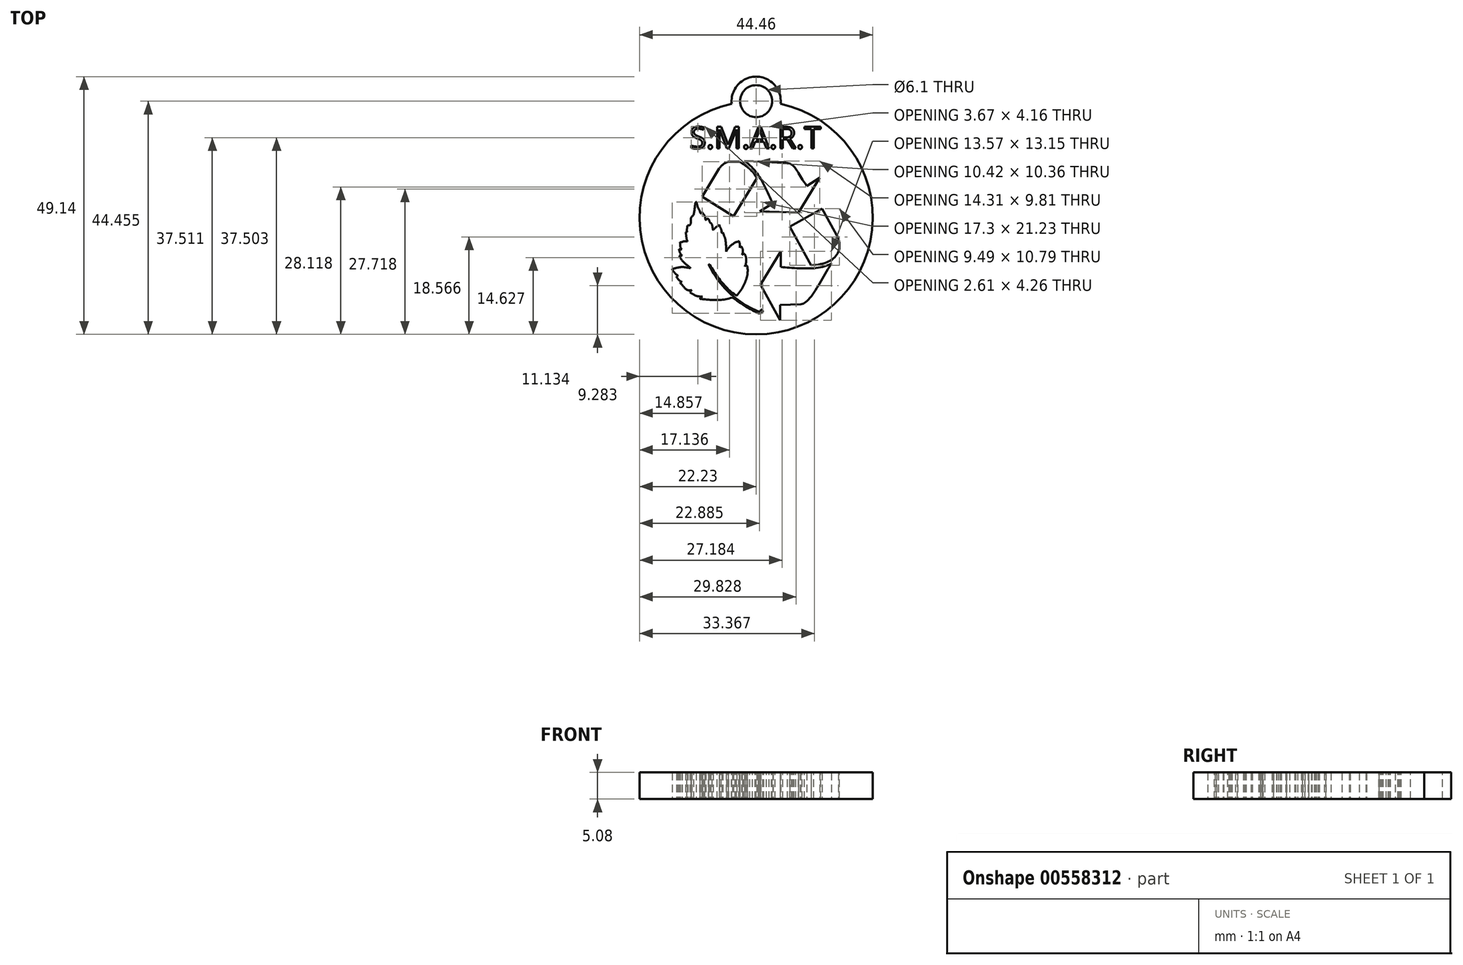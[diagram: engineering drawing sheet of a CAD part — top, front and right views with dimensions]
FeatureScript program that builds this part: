
annotation { "Feature Type Name" : "Feature", "Feature Type Description" : "" }
export const myFeature = defineFeature(function(context is Context, id is Id, definition is map)
    precondition{}
    {
        {
            var Q0;
            Q0=qCreatedBy(makeId("Top.planeOp"),FACE);
            var sketch = newSketch(context, id + "F0", { "sketchPlane" : qUnion([Q0])});
            skCircle(sketch, "E0", {"center": v(0, 0) * mm, "radius": 22.23 * mm});
            skLineSegment(sketch, "E1", {"start": v(4.56, -19.52) * mm, "end": v(4.56, -16.6) * mm});
            skLineSegment(sketch, "E2", {"start": v(4.56, -19.52) * mm, "end": v(0.81, -12.74) * mm});
            skLineSegment(sketch, "E3", {"start": v(0.81, -12.74) * mm, "end": v(4.68, -6.37) * mm});
            skLineSegment(sketch, "E4", {"start": v(4.68, -6.37) * mm, "end": v(4.68, -9.38) * mm});
            skFitSpline(sketch, "E5", {"points": [v(4.68, -9.38) * mm, v(14.38, -8.68) * mm], "startDerivative": vector(9.07, -0.86) * mm, "endDerivative": vector(6.6, 4.16) * mm});
            skFitSpline(sketch, "E6", {"points": [v(14.38, -8.68) * mm, v(8.52, -16.48) * mm], "startDerivative": vector(-5.26, -7.9) * mm, "endDerivative": vector(-5.23, 0.16) * mm});
            skLineSegment(sketch, "E7", {"start": v(8.52, -16.48) * mm, "end": v(4.56, -16.6) * mm});
            skLineSegment(sketch, "E8", {"start": v(10.48, -9.06) * mm, "end": v(6.4, -1.67) * mm});
            skLineSegment(sketch, "E9", {"start": v(6.4, -1.67) * mm, "end": v(12.54, 1.73) * mm});
            skFitSpline(sketch, "E10", {"points": [v(10.48, -9.06) * mm, v(15.66, -3.9) * mm], "startDerivative": vector(11.37, 0.62) * mm, "endDerivative": vector(-3, 9.99) * mm});
            skLineSegment(sketch, "E11", {"start": v(15.66, -3.9) * mm, "end": v(12.54, 1.73) * mm});
            skLineSegment(sketch, "E12", {"start": v(-10.3, 4) * mm, "end": v(-4.31, 0.3) * mm});
            skLineSegment(sketch, "E13", {"start": v(-4.31, 0.3) * mm, "end": v(0.12, 7.49) * mm});
            skFitSpline(sketch, "E14", {"points": [v(0.12, 7.49) * mm, v(-3.15, 10.67) * mm], "startDerivative": vector(-1.7, 4.08) * mm, "endDerivative": vector(-4.05, 2.48) * mm});
            skLineSegment(sketch, "E15", {"start": v(-3.15, 10.67) * mm, "end": v(-5.34, 10.67) * mm});
            skFitSpline(sketch, "E16", {"points": [v(-5.34, 10.67) * mm, v(-7.03, 9.39) * mm], "startDerivative": vector(-1.77, -0.76) * mm, "endDerivative": vector(-1.77, -2.58) * mm});
            skLineSegment(sketch, "E17", {"start": v(-7.03, 9.39) * mm, "end": v(-10.3, 4) * mm});
            skLineSegment(sketch, "E18", {"start": v(3.14, 2.73) * mm, "end": v(0.67, 1.2) * mm});
            skLineSegment(sketch, "E19", {"start": v(0.67, 1.2) * mm, "end": v(8.09, 0.98) * mm});
            skLineSegment(sketch, "E20", {"start": v(8.09, 0.98) * mm, "end": v(12.1, 7.65) * mm});
            skLineSegment(sketch, "E21", {"start": v(12.1, 7.65) * mm, "end": v(9.67, 6.06) * mm});
            skFitSpline(sketch, "E22", {"points": [v(3.14, 2.73) * mm, v(-2.2, 10.8) * mm], "startDerivative": vector(-4.28, 9.41) * mm, "endDerivative": vector(-8.22, 5.58) * mm});
            skFitSpline(sketch, "E23", {"points": [v(9.67, 6.06) * mm, v(4.61, 10.58) * mm], "startDerivative": vector(-7.32, 10) * mm, "endDerivative": vector(-9.47, 0.24) * mm});
            skLineSegment(sketch, "E24", {"start": v(-2.2, 10.8) * mm, "end": v(4.61, 10.58) * mm});
            skFitSpline(sketch, "E25", {"points": [v(-3.67, -14.85) * mm, v(-1.7, -9.2) * mm], "startDerivative": vector(4.77, 6.12) * mm, "endDerivative": vector(-1.06, 5.4) * mm});
            skFitSpline(sketch, "E26", {"points": [v(-1.7, -9.2) * mm, v(-2.15, -9.23) * mm], "startDerivative": vector(-0.44, 0.64) * mm, "endDerivative": vector(-0.19, -0.24) * mm});
            skFitSpline(sketch, "E27", {"points": [v(-2.15, -9.23) * mm, v(-2.15, -6.94) * mm], "startDerivative": vector(1.11, 1.98) * mm, "endDerivative": vector(-1.03, 1.88) * mm});
            skFitSpline(sketch, "E28", {"points": [v(-2.15, -6.94) * mm, v(-2.68, -7.06) * mm], "startDerivative": vector(-0.4, 0.22) * mm, "endDerivative": vector(-0.6, -0.4) * mm});
            skFitSpline(sketch, "E29", {"points": [v(-2.68, -7.06) * mm, v(-2.8, -5.47) * mm], "startDerivative": vector(0.95, 2.83) * mm, "endDerivative": vector(-0.62, 1.32) * mm});
            skFitSpline(sketch, "E30", {"points": [v(-2.8, -5.47) * mm, v(-3.11, -5.7) * mm], "startDerivative": vector(-0.32, -0.12) * mm, "endDerivative": vector(-0.33, -0.48) * mm});
            skFitSpline(sketch, "E31", {"points": [v(-3.11, -5.7) * mm, v(-3.26, -4.45) * mm], "startDerivative": vector(0.33, 1.85) * mm, "endDerivative": vector(-0.16, 0.95) * mm});
            skFitSpline(sketch, "E32", {"points": [v(-3.26, -4.45) * mm, v(-5.71, -6.44) * mm], "startDerivative": vector(-3.06, -0.88) * mm, "endDerivative": vector(-1.38, -2.86) * mm});
            skFitSpline(sketch, "E33", {"points": [v(-5.71, -6.44) * mm, v(-6.38, -2.8) * mm], "startDerivative": vector(-0.1, 6.22) * mm, "endDerivative": vector(-1.67, 3.3) * mm});
            skFitSpline(sketch, "E34", {"points": [v(-6.56, -2.96) * mm, v(-6.98, -1.34) * mm], "startDerivative": vector(-0.12, 3.42) * mm, "endDerivative": vector(0.03, 1.58) * mm});
            skFitSpline(sketch, "E35", {"points": [v(-6.98, -1.34) * mm, v(-8.21, -2.35) * mm], "startDerivative": vector(-1.42, -0.86) * mm, "endDerivative": vector(-1.17, -1.37) * mm});
            skFitSpline(sketch, "E36", {"points": [v(-8.21, -2.35) * mm, v(-8.63, -0.98) * mm], "startDerivative": vector(-0.57, 2) * mm, "endDerivative": vector(-1.08, 1.1) * mm});
            skFitSpline(sketch, "E37", {"points": [v(-8.63, -0.98) * mm, v(-9.07, -0.27) * mm], "startDerivative": vector(-0.72, -0.21) * mm, "endDerivative": vector(-0.36, 0.32) * mm});
            skFitSpline(sketch, "E38", {"points": [v(-9.07, -0.27) * mm, v(-9.59, -0.42) * mm], "startDerivative": vector(-0.38, 0.47) * mm, "endDerivative": vector(-0.6, -0.75) * mm});
            skFitSpline(sketch, "E39", {"points": [v(-9.59, -0.42) * mm, v(-9.8, 0.34) * mm], "startDerivative": vector(-0.42, 0.2) * mm, "endDerivative": vector(-0.4, 0.6) * mm});
            skFitSpline(sketch, "E40", {"points": [v(-9.8, 0.34) * mm, v(-10.3, 1.04) * mm], "startDerivative": vector(-0.37, 0.79) * mm, "endDerivative": vector(-0.6, 0.7) * mm});
            skFitSpline(sketch, "E41", {"points": [v(-10.3, 1.04) * mm, v(-10.53, 0.78) * mm], "startDerivative": vector(-0.35, -0.1) * mm, "endDerivative": vector(-0.14, -0.5) * mm});
            skFitSpline(sketch, "E42", {"points": [v(-10.53, 0.78) * mm, v(-10.81, 1.49) * mm], "startDerivative": vector(-0.46, 0.36) * mm, "endDerivative": vector(-0.28, 0.7) * mm});
            skFitSpline(sketch, "E43", {"points": [v(-10.81, 1.49) * mm, v(-11.44, 3.01) * mm], "startDerivative": vector(-1.4, 1.16) * mm, "endDerivative": vector(-0.57, -0.16) * mm});
            skFitSpline(sketch, "E44", {"points": [v(-11.44, 3.01) * mm, v(-12.3, 0.23) * mm], "startDerivative": vector(-1.03, 0.25) * mm, "endDerivative": vector(-2.13, -0.16) * mm});
            skFitSpline(sketch, "E45", {"points": [v(-12.3, 0.23) * mm, v(-13.04, -1.42) * mm], "startDerivative": vector(-1.19, -1.35) * mm, "endDerivative": vector(-2.9, 0.55) * mm});
            skFitSpline(sketch, "E46", {"points": [v(-13.04, -1.42) * mm, v(-13.17, -2.73) * mm], "startDerivative": vector(-0.45, -0.86) * mm, "endDerivative": vector(0.1, -1.6) * mm});
            skFitSpline(sketch, "E47", {"points": [v(-13.17, -2.73) * mm, v(-13.45, -2.73) * mm], "startDerivative": vector(-0.28, 0) * mm, "endDerivative": vector(-0.28, 0) * mm});
            skFitSpline(sketch, "E48", {"points": [v(-13.45, -2.73) * mm, v(-13.08, -4.47) * mm], "startDerivative": vector(0.43, -1.93) * mm, "endDerivative": vector(0.73, -1.04) * mm});
            skFitSpline(sketch, "E49", {"points": [v(-13.08, -4.47) * mm, v(-14.55, -4.66) * mm], "startDerivative": vector(-3.85, 0.16) * mm, "endDerivative": vector(-2.6, -0.02) * mm});
            skFitSpline(sketch, "E50", {"points": [v(-14.55, -4.66) * mm, v(-14.16, -6.04) * mm], "startDerivative": vector(0.52, -1.16) * mm, "endDerivative": vector(1.45, -1.38) * mm});
            skFitSpline(sketch, "E51", {"points": [v(-14.16, -6.04) * mm, v(-14.75, -6.04) * mm], "startDerivative": vector(-0.59, 0) * mm, "endDerivative": vector(-0.59, 0) * mm});
            skFitSpline(sketch, "E52", {"points": [v(-14.75, -6.04) * mm, v(-14.1, -7.23) * mm], "startDerivative": vector(0.65, -1.2) * mm, "endDerivative": vector(1.5, -1.23) * mm});
            skFitSpline(sketch, "E53", {"points": [v(-14.1, -7.23) * mm, v(-14.67, -7.23) * mm], "startDerivative": vector(-0.57, 0) * mm, "endDerivative": vector(-0.57, 0) * mm});
            skFitSpline(sketch, "E54", {"points": [v(-14.67, -7.23) * mm, v(-12.48, -9.63) * mm], "startDerivative": vector(1.06, -2.87) * mm, "endDerivative": vector(2.75, -2.45) * mm});
            skFitSpline(sketch, "E55", {"points": [v(-12.48, -9.63) * mm, v(-16.03, -9.77) * mm], "startDerivative": vector(-6.32, 1.51) * mm, "endDerivative": vector(-3.02, -0.57) * mm});
            skFitSpline(sketch, "E56", {"points": [v(-16.03, -9.77) * mm, v(-14.95, -11) * mm], "startDerivative": vector(1, -1.77) * mm, "endDerivative": vector(1.47, -0.94) * mm});
            skFitSpline(sketch, "E57", {"points": [v(-14.95, -11) * mm, v(-15.2, -11.27) * mm], "startDerivative": vector(-0.05, -0.46) * mm, "endDerivative": vector(-0.24, -0.27) * mm});
            skFitSpline(sketch, "E58", {"points": [v(-15.2, -11.27) * mm, v(-14.18, -12.2) * mm], "startDerivative": vector(0.81, -1.06) * mm, "endDerivative": vector(1.3, -0.3) * mm});
            skFitSpline(sketch, "E59", {"points": [v(-14.18, -12.2) * mm, v(-14.48, -12.48) * mm], "startDerivative": vector(-0.6, -0.17) * mm, "endDerivative": vector(-0.3, -0.27) * mm});
            skFitSpline(sketch, "E60", {"points": [v(-14.48, -12.48) * mm, v(-12.29, -13.77) * mm], "startDerivative": vector(2.29, -1.72) * mm, "endDerivative": vector(3.61, 1) * mm});
            skFitSpline(sketch, "E61", {"points": [v(-12.29, -13.77) * mm, v(-12.62, -14.23) * mm], "startDerivative": vector(-0.33, -0.46) * mm, "endDerivative": vector(-0.2, -0.77) * mm});
            skFitSpline(sketch, "E62", {"points": [v(-12.62, -14.23) * mm, v(-10.21, -15.06) * mm], "startDerivative": vector(2.34, -1.06) * mm, "endDerivative": vector(4.73, -0.17) * mm});
            skFitSpline(sketch, "E63", {"points": [v(-10.21, -15.06) * mm, v(-10.66, -15.31) * mm], "startDerivative": vector(-0.45, -0.26) * mm, "endDerivative": vector(-0.45, -0.26) * mm});
            skFitSpline(sketch, "E64", {"points": [v(-10.66, -15.31) * mm, v(-10.63, -15.49) * mm], "startDerivative": vector(-0.2, -0.25) * mm, "endDerivative": vector(0.18, -0.08) * mm});
            skFitSpline(sketch, "E65", {"points": [v(-10.63, -15.49) * mm, v(-4.53, -15.19) * mm], "startDerivative": vector(5.21, -0.17) * mm, "endDerivative": vector(7.83, 2.62) * mm});
            skFitSpline(sketch, "E66", {"points": [v(-4.53, -15.19) * mm, v(0.21, -18.1) * mm], "startDerivative": vector(4.25, -3.24) * mm, "endDerivative": vector(4.65, -2.18) * mm});
            skFitSpline(sketch, "E67", {"points": [v(0.21, -18.1) * mm, v(0.9, -17.47) * mm], "startDerivative": vector(2.35, -1.32) * mm, "endDerivative": vector(-2.65, 0.54) * mm});
            skFitSpline(sketch, "E68", {"points": [v(0.9, -17.47) * mm, v(0.31, -17.8) * mm], "startDerivative": vector(0, -1.02) * mm, "endDerivative": vector(-0.93, 0.51) * mm});
            skFitSpline(sketch, "E69", {"points": [v(0.31, -17.8) * mm, v(-9, -9) * mm], "startDerivative": vector(-11.16, 4.58) * mm, "endDerivative": vector(-6.38, 12.86) * mm});
            skFitSpline(sketch, "E70", {"points": [v(-9, -9) * mm, v(-8.83, -9) * mm], "startDerivative": vector(-0.1, 0.45) * mm, "endDerivative": vector(0.3, -0.43) * mm});
            skFitSpline(sketch, "E71", {"points": [v(-8.83, -9) * mm, v(-3.67, -14.85) * mm], "startDerivative": vector(4.25, -6.74) * mm, "endDerivative": vector(6.44, -3.7) * mm});
            skFitSpline(sketch, "E72", {"points": [v(-6.56, -2.96) * mm, v(-6.38, -2.8) * mm], "startDerivative": vector(0.24, 0.28) * mm, "endDerivative": vector(0.37, 0.05) * mm});
            skSolve(sketch);
        }
        {
            var Q0;
            Q0 = qSketchRegion(id + "F0", true);
            extrude(context, id + "F1", {"entities" : qUnion([Q0]), "depth" : 5.08 * mm, "offsetDistance" : 25.4 * mm});
        }
        {
            var Q0;
            Q0=makeQuery(id+"F1.opExtrude","CAP_FACE",FACE,{"disambiguationData":[OSD([sQuery(id+"F0.wireOp",EDGE,"E0"),sQuery(id+"F0.wireOp",EDGE,"E1"),sQuery(id+"F0.wireOp",EDGE,"E2"),sQuery(id+"F0.wireOp",EDGE,"E3"),sQuery(id+"F0.wireOp",EDGE,"E4"),sQuery(id+"F0.wireOp",EDGE,"E5"),sQuery(id+"F0.wireOp",EDGE,"E6"),sQuery(id+"F0.wireOp",EDGE,"E7"),sQuery(id+"F0.wireOp",EDGE,"E8"),sQuery(id+"F0.wireOp",EDGE,"E9"),sQuery(id+"F0.wireOp",EDGE,"E10"),sQuery(id+"F0.wireOp",EDGE,"E11"),sQuery(id+"F0.wireOp",EDGE,"E12"),sQuery(id+"F0.wireOp",EDGE,"E13"),sQuery(id+"F0.wireOp",EDGE,"E14"),sQuery(id+"F0.wireOp",EDGE,"E15"),sQuery(id+"F0.wireOp",EDGE,"E16"),sQuery(id+"F0.wireOp",EDGE,"E17"),sQuery(id+"F0.wireOp",EDGE,"E18"),sQuery(id+"F0.wireOp",EDGE,"E19"),sQuery(id+"F0.wireOp",EDGE,"E20"),sQuery(id+"F0.wireOp",EDGE,"E21"),sQuery(id+"F0.wireOp",EDGE,"E22"),sQuery(id+"F0.wireOp",EDGE,"E23"),sQuery(id+"F0.wireOp",EDGE,"E24"),sQuery(id+"F0.wireOp",EDGE,"E25"),sQuery(id+"F0.wireOp",EDGE,"E26"),sQuery(id+"F0.wireOp",EDGE,"E27"),sQuery(id+"F0.wireOp",EDGE,"E28"),sQuery(id+"F0.wireOp",EDGE,"E29"),sQuery(id+"F0.wireOp",EDGE,"E30"),sQuery(id+"F0.wireOp",EDGE,"E31"),sQuery(id+"F0.wireOp",EDGE,"E32"),sQuery(id+"F0.wireOp",EDGE,"E33"),sQuery(id+"F0.wireOp",EDGE,"E34"),sQuery(id+"F0.wireOp",EDGE,"E35"),sQuery(id+"F0.wireOp",EDGE,"E36"),sQuery(id+"F0.wireOp",EDGE,"E37"),sQuery(id+"F0.wireOp",EDGE,"E38"),sQuery(id+"F0.wireOp",EDGE,"E39"),sQuery(id+"F0.wireOp",EDGE,"E40"),sQuery(id+"F0.wireOp",EDGE,"E41"),sQuery(id+"F0.wireOp",EDGE,"E42"),sQuery(id+"F0.wireOp",EDGE,"E43"),sQuery(id+"F0.wireOp",EDGE,"E44"),sQuery(id+"F0.wireOp",EDGE,"E45"),sQuery(id+"F0.wireOp",EDGE,"E46"),sQuery(id+"F0.wireOp",EDGE,"E47"),sQuery(id+"F0.wireOp",EDGE,"E48"),sQuery(id+"F0.wireOp",EDGE,"E49"),sQuery(id+"F0.wireOp",EDGE,"E50"),sQuery(id+"F0.wireOp",EDGE,"E51"),sQuery(id+"F0.wireOp",EDGE,"E52"),sQuery(id+"F0.wireOp",EDGE,"E53"),sQuery(id+"F0.wireOp",EDGE,"E54"),sQuery(id+"F0.wireOp",EDGE,"E55"),sQuery(id+"F0.wireOp",EDGE,"E56"),sQuery(id+"F0.wireOp",EDGE,"E57"),sQuery(id+"F0.wireOp",EDGE,"E58"),sQuery(id+"F0.wireOp",EDGE,"E59"),sQuery(id+"F0.wireOp",EDGE,"E60"),sQuery(id+"F0.wireOp",EDGE,"E61"),sQuery(id+"F0.wireOp",EDGE,"E62"),sQuery(id+"F0.wireOp",EDGE,"E63"),sQuery(id+"F0.wireOp",EDGE,"E64"),sQuery(id+"F0.wireOp",EDGE,"E65"),sQuery(id+"F0.wireOp",EDGE,"E66"),sQuery(id+"F0.wireOp",EDGE,"E67"),sQuery(id+"F0.wireOp",EDGE,"E68"),sQuery(id+"F0.wireOp",EDGE,"E69"),sQuery(id+"F0.wireOp",EDGE,"E70"),sQuery(id+"F0.wireOp",EDGE,"E71"),sQuery(id+"F0.wireOp",EDGE,"E72")])],"isStart":false});
            var sketch = newSketch(context, id + "F2", { "sketchPlane" : qUnion([Q0])});
            skText(sketch, "E73", { "text": "S.M.A.R.T", "fontName": "OpenSans-Regular.ttf"});
            const initialGuessF2  = {"E73": [-0.0127, 0.0132, 1, 0, 0.00418]};
            skSetInitialGuess(sketch, initialGuessF2);
            skSolve(sketch);
        }
        {
            var Q0;
            Q0 = qSketchRegion(id + "F2", true);
            extrude(context, id + "F3", {"entities" : qUnion([Q0]), "operationType" : NewBodyOperationType.REMOVE, "oppositeDirection" : true, "depth" : 25.4 * mm, "offsetDistance" : 25.4 * mm});
        }
        {
            var Q0;
            {var subQ0=sQuery(id+"F0.wireOp",EDGE,"E72");var subQ1=sQuery(id+"F0.wireOp",EDGE,"E71");var subQ2=sQuery(id+"F0.wireOp",EDGE,"E70");var subQ3=sQuery(id+"F0.wireOp",EDGE,"E69");var subQ4=sQuery(id+"F0.wireOp",EDGE,"E68");var subQ5=sQuery(id+"F0.wireOp",EDGE,"E67");var subQ6=sQuery(id+"F0.wireOp",EDGE,"E66");var subQ7=sQuery(id+"F0.wireOp",EDGE,"E65");var subQ8=sQuery(id+"F0.wireOp",EDGE,"E64");var subQ9=sQuery(id+"F0.wireOp",EDGE,"E63");var subQ10=sQuery(id+"F0.wireOp",EDGE,"E62");var subQ11=sQuery(id+"F0.wireOp",EDGE,"E61");var subQ12=sQuery(id+"F0.wireOp",EDGE,"E60");var subQ13=sQuery(id+"F0.wireOp",EDGE,"E59");var subQ14=sQuery(id+"F0.wireOp",EDGE,"E58");var subQ15=sQuery(id+"F0.wireOp",EDGE,"E57");var subQ16=sQuery(id+"F0.wireOp",EDGE,"E56");var subQ17=sQuery(id+"F0.wireOp",EDGE,"E55");var subQ18=sQuery(id+"F0.wireOp",EDGE,"E54");var subQ19=sQuery(id+"F0.wireOp",EDGE,"E53");var subQ20=sQuery(id+"F0.wireOp",EDGE,"E52");var subQ21=sQuery(id+"F0.wireOp",EDGE,"E51");var subQ22=sQuery(id+"F0.wireOp",EDGE,"E50");var subQ23=sQuery(id+"F0.wireOp",EDGE,"E49");var subQ24=sQuery(id+"F0.wireOp",EDGE,"E48");var subQ25=sQuery(id+"F0.wireOp",EDGE,"E47");var subQ26=sQuery(id+"F0.wireOp",EDGE,"E46");var subQ27=sQuery(id+"F0.wireOp",EDGE,"E29");var subQ28=sQuery(id+"F0.wireOp",EDGE,"E20");var subQ29=sQuery(id+"F0.wireOp",EDGE,"E28");var subQ30=sQuery(id+"F0.wireOp",EDGE,"E19");var subQ31=sQuery(id+"F0.wireOp",EDGE,"E18");var subQ32=sQuery(id+"F0.wireOp",EDGE,"E17");var subQ33=sQuery(id+"F0.wireOp",EDGE,"E25");var subQ34=sQuery(id+"F0.wireOp",EDGE,"E16");var subQ35=sQuery(id+"F0.wireOp",EDGE,"E15");var subQ36=sQuery(id+"F0.wireOp",EDGE,"E14");var subQ37=sQuery(id+"F0.wireOp",EDGE,"E13");var subQ38=sQuery(id+"F0.wireOp",EDGE,"E12");var subQ39=sQuery(id+"F0.wireOp",EDGE,"E11");var subQ40=sQuery(id+"F0.wireOp",EDGE,"E10");var subQ41=sQuery(id+"F0.wireOp",EDGE,"E2");var subQ42=sQuery(id+"F0.wireOp",EDGE,"E1");var subQ43=sQuery(id+"F0.wireOp",EDGE,"E3");var subQ44=sQuery(id+"F0.wireOp",EDGE,"E30");var subQ45=sQuery(id+"F0.wireOp",EDGE,"E21");var subQ46=sQuery(id+"F0.wireOp",EDGE,"E0");var subQ47=sQuery(id+"F0.wireOp",EDGE,"E45");var subQ48=sQuery(id+"F0.wireOp",EDGE,"E9");var subQ49=sQuery(id+"F0.wireOp",EDGE,"E4");var subQ50=sQuery(id+"F0.wireOp",EDGE,"E5");var subQ51=sQuery(id+"F0.wireOp",EDGE,"E6");var subQ52=sQuery(id+"F0.wireOp",EDGE,"E7");var subQ53=sQuery(id+"F0.wireOp",EDGE,"E8");var subQ54=sQuery(id+"F0.wireOp",EDGE,"E31");var subQ55=sQuery(id+"F0.wireOp",EDGE,"E22");var subQ56=sQuery(id+"F0.wireOp",EDGE,"E32");var subQ57=sQuery(id+"F0.wireOp",EDGE,"E23");var subQ58=sQuery(id+"F0.wireOp",EDGE,"E33");var subQ59=sQuery(id+"F0.wireOp",EDGE,"E24");var subQ60=sQuery(id+"F0.wireOp",EDGE,"E34");var subQ61=sQuery(id+"F0.wireOp",EDGE,"E35");var subQ62=sQuery(id+"F0.wireOp",EDGE,"E26");var subQ63=sQuery(id+"F0.wireOp",EDGE,"E36");var subQ64=sQuery(id+"F0.wireOp",EDGE,"E27");var subQ65=sQuery(id+"F0.wireOp",EDGE,"E37");var subQ66=sQuery(id+"F0.wireOp",EDGE,"E38");var subQ67=sQuery(id+"F0.wireOp",EDGE,"E39");var subQ68=sQuery(id+"F0.wireOp",EDGE,"E40");var subQ69=sQuery(id+"F0.wireOp",EDGE,"E41");var subQ70=sQuery(id+"F0.wireOp",EDGE,"E42");var subQ71=sQuery(id+"F0.wireOp",EDGE,"E43");var subQ72=sQuery(id+"F0.wireOp",EDGE,"E44");Q0=makeQuery(id+"F3.boolean.opBoolean","SPLIT",FACE,{"disambiguationData":[TD([makeQuery(id+"F1.opExtrude","SWEPT_FACE",FACE,{"disambiguationData":[OSD([subQ46])]})])],"derivedFrom":makeQuery(id+"F1.opExtrude","CAP_FACE",FACE,{"disambiguationData":[OSD([subQ46,subQ42,subQ41,subQ43,subQ49,subQ50,subQ51,subQ52,subQ53,subQ48,subQ40,subQ39,subQ38,subQ37,subQ36,subQ35,subQ34,subQ32,subQ31,subQ30,subQ28,subQ45,subQ55,subQ57,subQ59,subQ33,subQ62,subQ64,subQ29,subQ27,subQ44,subQ54,subQ56,subQ58,subQ60,subQ61,subQ63,subQ65,subQ66,subQ67,subQ68,subQ69,subQ70,subQ71,subQ72,subQ47,subQ26,subQ25,subQ24,subQ23,subQ22,subQ21,subQ20,subQ19,subQ18,subQ17,subQ16,subQ15,subQ14,subQ13,subQ12,subQ11,subQ10,subQ9,subQ8,subQ7,subQ6,subQ5,subQ4,subQ3,subQ2,subQ1,subQ0])],"isStart":false})});}
            var sketch = newSketch(context, id + "F4", { "sketchPlane" : qUnion([Q0])});
            skCircle(sketch, "E74", {"center": v(0, 22.23) * mm, "radius": 3.05 * mm});
            skCircle(sketch, "E75", {"center": v(0, 22.23) * mm, "radius": 4.68 * mm});
            skSolve(sketch);
        }
        {
            var Q0;
            Q0 = qSketchRegion(id + "F4", true);
            extrude(context, id + "F5", {"entities" : qUnion([Q0]), "operationType" : NewBodyOperationType.ADD, "oppositeDirection" : true, "depth" : 5.08 * mm, "offsetDistance" : 25.4 * mm});
        }
        {
            var Q0;
            {var subQ0=sQuery(id+"F4.wireOp",EDGE,"E74");var subQ1=makeQuery(id+"F1.opExtrude","CAP_EDGE",EDGE,{"disambiguationData":[OSD([sQuery(id+"F0.wireOp",EDGE,"E0")])],"isStart":false});var subQ2=makeQuery(id+"F4.imprint","INTERSECT",VERTEX,{"disambiguationData":[OD(0.0)],"derivedFrom":[subQ1,subQ0]});Q0=makeQuery(id+"F4.imprint","IMPRINT",FACE,{"disambiguationData":[TD([[makeQuery(id+"F4.imprint","IMPRINT",EDGE,{"disambiguationData":[TD([[subQ2,-1.0]])],"derivedFrom":subQ0}),1.0]])]});}
            extrude(context, id + "F6", {"entities" : qUnion([Q0]), "operationType" : NewBodyOperationType.REMOVE, "oppositeDirection" : true, "depth" : 25.4 * mm, "offsetDistance" : 25.4 * mm});
        }
    });
